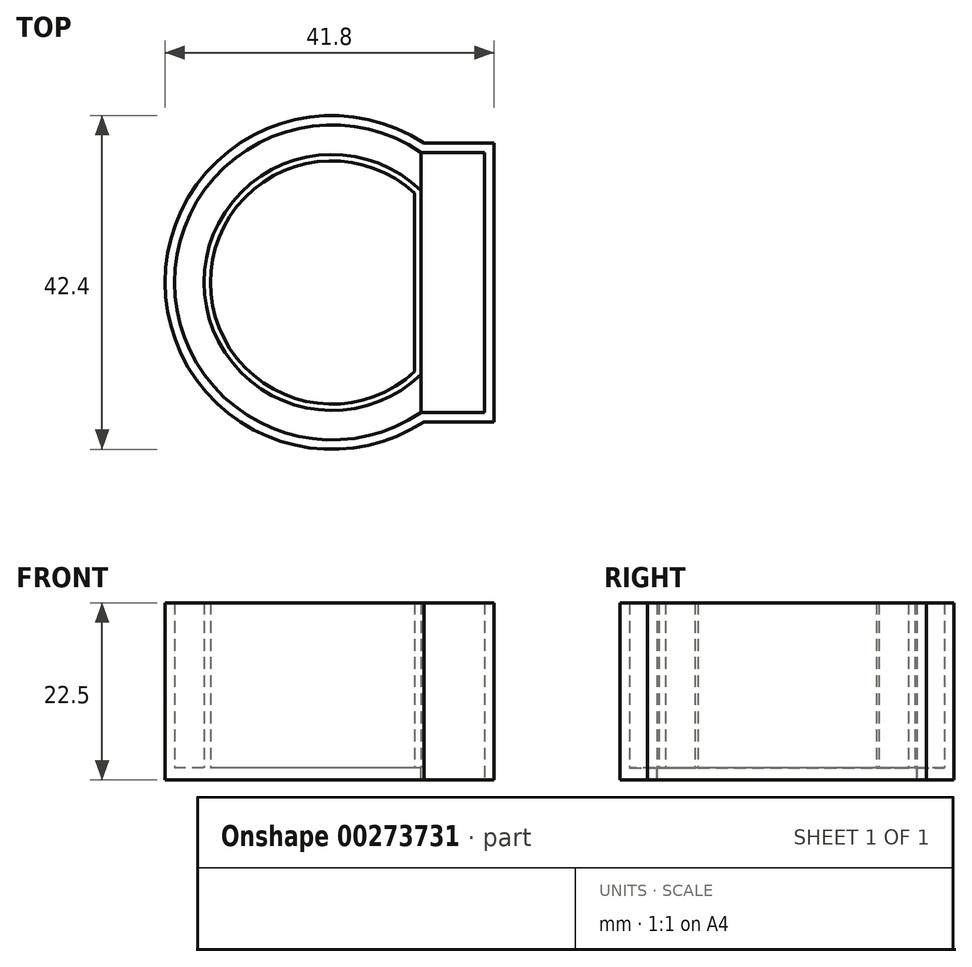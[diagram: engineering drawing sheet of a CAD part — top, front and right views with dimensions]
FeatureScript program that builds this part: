
annotation { "Feature Type Name" : "Feature", "Feature Type Description" : "" }
export const myFeature = defineFeature(function(context is Context, id is Id, definition is map)
    precondition{}
    {
        {
            var Q0;
            Q0=qCreatedBy(makeId("Top.planeOp"),FACE);
            var sketch = newSketch(context, id + "F0", { "sketchPlane" : qUnion([Q0])});
            skArc(sketch, "E0.0", {"start": v(11.3, 16.5) * mm, "mid": v(-20, 0) * mm, "end": v(11.3, -16.5) * mm, "construction": true});
            skLineSegment(sketch, "E1.0", {"start": v(11.3, 16.5) * mm, "end": v(19.4, 16.5) * mm, "construction": true});
            skLineSegment(sketch, "E2.0", {"start": v(19.4, 16.5) * mm, "end": v(19.4, -16.5) * mm, "construction": true});
            skLineSegment(sketch, "E3.0", {"start": v(11.3, -16.5) * mm, "end": v(19.4, -16.5) * mm, "construction": true});
            skPoint(sketch, "E4", {"position": v(19.4, 0) * mm});
            skLineSegment(sketch, "E5", {"start": v(0, 0) * mm, "end": v(19.4, 0) * mm, "construction": true});
            skArc(sketch, "E6.0", {"start": v(11.3, 16.5) * mm, "mid": v(-20, 0) * mm, "end": v(11.3, -16.5) * mm});
            skLineSegment(sketch, "E6.1", {"start": v(11.3, 16.5) * mm, "end": v(19.4, 16.5) * mm});
            skLineSegment(sketch, "E6.2", {"start": v(19.4, 16.5) * mm, "end": v(19.4, -16.5) * mm});
            skLineSegment(sketch, "E6.3", {"start": v(11.3, -16.5) * mm, "end": v(19.4, -16.5) * mm});
            skArc(sketch, "E7.0", {"start": v(11.67, 17.7) * mm, "mid": v(-21.2, 0) * mm, "end": v(11.67, -17.7) * mm});
            skLineSegment(sketch, "E7.1", {"start": v(11.67, 17.7) * mm, "end": v(20.6, 17.7) * mm});
            skLineSegment(sketch, "E7.2", {"start": v(20.6, 17.7) * mm, "end": v(20.6, -17.7) * mm});
            skLineSegment(sketch, "E7.3", {"start": v(11.67, -17.7) * mm, "end": v(20.6, -17.7) * mm});
            skCircle(sketch, "E8", {"center": v(0, 0) * mm, "radius": 16.25 * mm, "construction": true});
            skLineSegment(sketch, "E9", {"start": v(11.3, 16.5) * mm, "end": v(11.3, -16.5) * mm, "construction": true});
            skCircle(sketch, "E10", {"center": v(0, 0) * mm, "radius": 15.45 * mm, "construction": true});
            skLineSegment(sketch, "E11", {"start": v(11.3, 11.68) * mm, "end": v(11.3, -11.68) * mm});
            skLineSegment(sketch, "E12", {"start": v(10.5, 11.33) * mm, "end": v(10.5, -11.33) * mm});
            skPoint(sketch, "E13", {"position": v(-16.25, 0) * mm});
            skPoint(sketch, "E14", {"position": v(-15.45, 0) * mm});
            skArc(sketch, "E15", {"start": v(11.3, 11.68) * mm, "mid": v(-16.25, 0) * mm, "end": v(11.3, -11.68) * mm});
            skArc(sketch, "E16", {"start": v(10.5, 11.33) * mm, "mid": v(-15.45, 0) * mm, "end": v(10.5, -11.33) * mm});
            skSolve(sketch);
        }
        {
            var Q0;
            Q0=makeQuery(id+"F0.imprint","IMPRINT",FACE,{"disambiguationData":[TD([[makeQuery(id+"F0.imprint","IMPRINT",EDGE,{"derivedFrom":sQuery(id+"F0.wireOp",EDGE,"E6.0")}),-1.0]])]});
            var Q1;
            Q1=makeQuery(id+"F0.imprint","IMPRINT",FACE,{"disambiguationData":[TD([[makeQuery(id+"F0.imprint","IMPRINT",EDGE,{"derivedFrom":sQuery(id+"F0.wireOp",EDGE,"f2ec96a0-f012-44b0-84ee-4daabd0e4c6e.0")}),1.0]])]});
            var Q2;
            Q2=makeQuery(id+"F0.imprint","IMPRINT",FACE,{"disambiguationData":[TD([[makeQuery(id+"F0.imprint","IMPRINT",EDGE,{"derivedFrom":sQuery(id+"F0.wireOp",EDGE,"E6.0")}),1.0]])]});
            var Q3;
            Q3=makeQuery(id+"F0.imprint","IMPRINT",FACE,{"disambiguationData":[TD([[makeQuery(id+"F0.imprint","IMPRINT",EDGE,{"derivedFrom":sQuery(id+"F0.wireOp",EDGE,"0c535ff1-adff-4964-a420-ab66b33d93f3.0")}),1.0]])]});
            var Q4;
            Q4=makeQuery(id+"F0.imprint","IMPRINT",FACE,{"disambiguationData":[TD([[makeQuery(id+"F0.imprint","IMPRINT",EDGE,{"derivedFrom":sQuery(id+"F0.wireOp",EDGE,"E12")}),-1.0]])]});
            var Q5;
            Q5=makeQuery(id+"F0.imprint","IMPRINT",FACE,{"disambiguationData":[TD([[makeQuery(id+"F0.imprint","IMPRINT",EDGE,{"derivedFrom":sQuery(id+"F0.wireOp",EDGE,"E11")}),-1.0]])]});
            extrude(context, id + "F1", {"entities" : qUnion([Q0, Q1, Q2, Q3, Q4, Q5]), "depth" : 1.5 * mm});
        }
        {
            var Q0;
            Q0=makeQuery(id+"F0.imprint","IMPRINT",FACE,{"disambiguationData":[TD([[makeQuery(id+"F0.imprint","IMPRINT",EDGE,{"derivedFrom":sQuery(id+"F0.wireOp",EDGE,"f2ec96a0-f012-44b0-84ee-4daabd0e4c6e.0")}),1.0]])]});
            var Q1;
            Q1=makeQuery(id+"F0.imprint","IMPRINT",FACE,{"disambiguationData":[TD([[makeQuery(id+"F0.imprint","IMPRINT",EDGE,{"derivedFrom":sQuery(id+"F0.wireOp",EDGE,"E6.0")}),-1.0]])]});
            var Q2;
            Q2=makeQuery(id+"F0.imprint","IMPRINT",FACE,{"disambiguationData":[TD([[makeQuery(id+"F0.imprint","IMPRINT",EDGE,{"derivedFrom":sQuery(id+"F0.wireOp",EDGE,"E11")}),-1.0]])]});
            extrude(context, id + "F2", {"entities" : qUnion([Q0, Q1, Q2]), "operationType" : NewBodyOperationType.ADD, "depth" : 22.5 * mm});
        }
        {
            var Q0;
            Q0=makeQuery(id+"F2.boolean.opBoolean","SPLIT",FACE,{"disambiguationData":[TD([makeQuery(id+"F2.opExtrude","SWEPT_FACE",FACE,{"disambiguationData":[OSD([sQuery(id+"F0.wireOp",EDGE,"E6.0")])]})])],"derivedFrom":makeQuery(id+"F1.opExtrude","CAP_FACE",FACE,{"disambiguationData":[OSD([sQuery(id+"F0.wireOp",EDGE,"E7.0"),sQuery(id+"F0.wireOp",EDGE,"E7.1"),sQuery(id+"F0.wireOp",EDGE,"E7.2"),sQuery(id+"F0.wireOp",EDGE,"E7.3")])],"isStart":false})});
            var sketch = newSketch(context, id + "F3", { "sketchPlane" : qUnion([Q0])});
            skLineSegment(sketch, "E17.0", {"start": v(11.3, 16.5) * mm, "end": v(19.4, 16.5) * mm});
            skLineSegment(sketch, "E18.0", {"start": v(19.4, 16.5) * mm, "end": v(19.4, -16.5) * mm});
            skLineSegment(sketch, "E19", {"start": v(11.3, 16.5) * mm, "end": v(11.3, -16.5) * mm});
            skSolve(sketch);
        }
        {
            var Q0;
            Q0=makeQuery(id+"F3.imprint","IMPRINT",FACE,{"disambiguationData":[TD([[makeQuery(id+"F3.imprint","IMPRINT",EDGE,{"derivedFrom":sQuery(id+"F3.wireOp",EDGE,"E17.0")}),1.0]])]});
            extrude(context, id + "F4", {"entities" : qUnion([Q0]), "operationType" : NewBodyOperationType.REMOVE, "oppositeDirection" : true, "depth" : 25 * mm});
        }
    });
